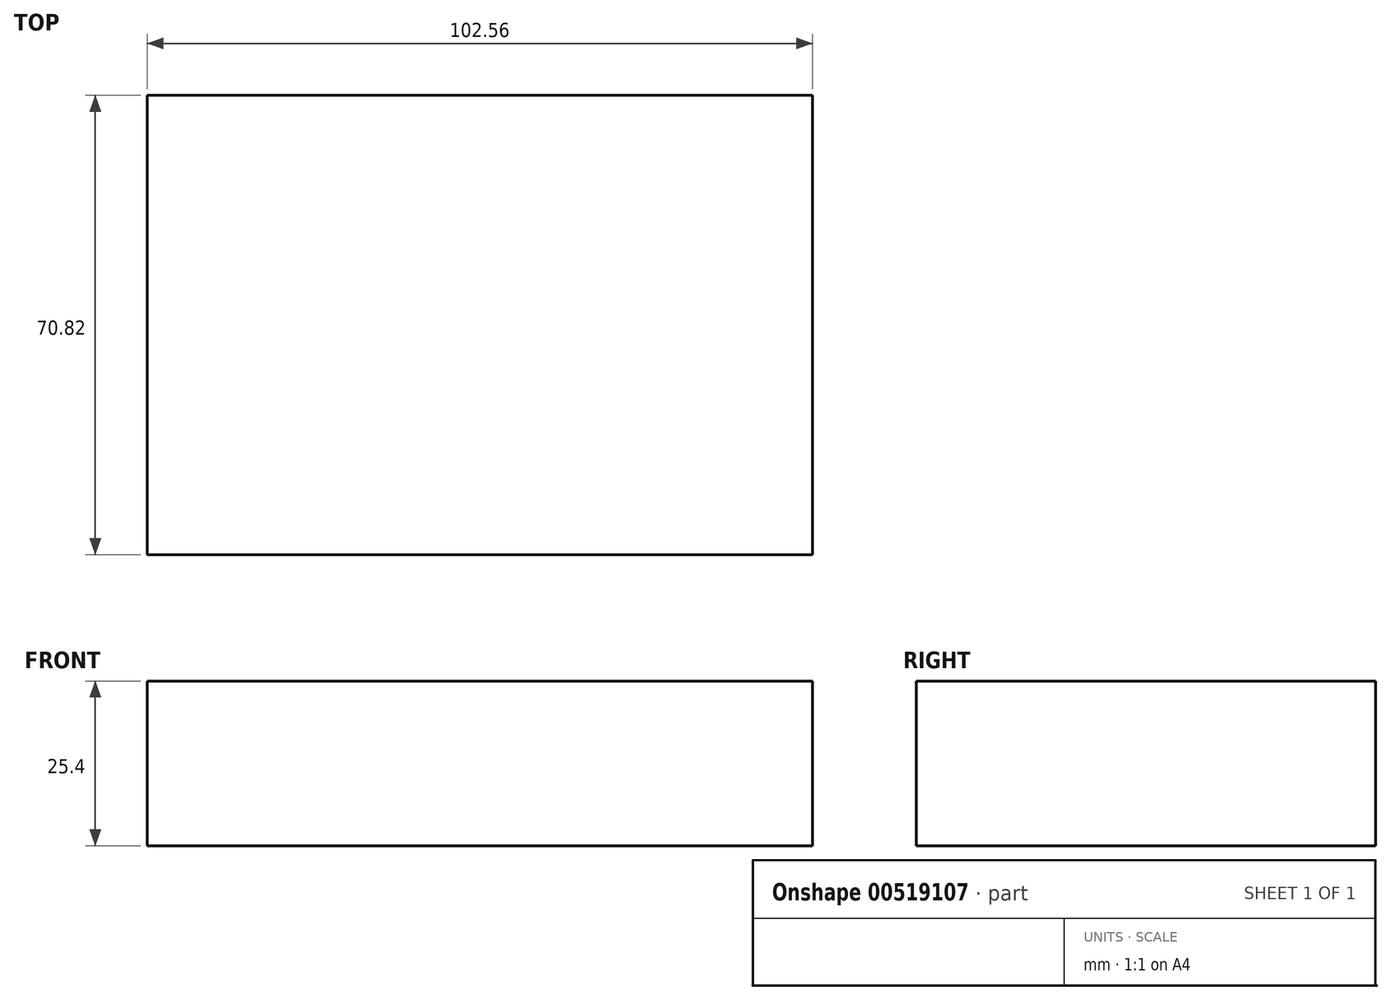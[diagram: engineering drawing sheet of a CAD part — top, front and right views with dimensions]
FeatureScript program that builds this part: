
annotation { "Feature Type Name" : "Feature", "Feature Type Description" : "" }
export const myFeature = defineFeature(function(context is Context, id is Id, definition is map)
    precondition{}
    {
        {
            var Q0;
            Q0=qCreatedBy(makeId("Top.planeOp"),FACE);
            var sketch = newSketch(context, id + "F0", { "sketchPlane" : qUnion([Q0])});
            skLineSegment(sketch, "E0.bottom", {"start": v(51.28, 35.41) * mm, "end": v(-51.28, 35.41) * mm});
            skLineSegment(sketch, "E0.top", {"start": v(51.28, -35.41) * mm, "end": v(-51.28, -35.41) * mm});
            skLineSegment(sketch, "E0.left", {"start": v(51.28, 35.41) * mm, "end": v(51.28, -35.41) * mm});
            skLineSegment(sketch, "E0.right", {"start": v(-51.28, 35.41) * mm, "end": v(-51.28, -35.41) * mm});
            skPoint(sketch, "E0.middle", {"position": v(0, 0) * mm});
            skSolve(sketch);
        }
        {
            var Q0;
            Q0=makeQuery(id+"F0.imprint","IMPRINT",FACE,{"disambiguationData":[TD([[makeQuery(id+"F0.imprint","IMPRINT",EDGE,{"derivedFrom":sQuery(id+"F0.wireOp",EDGE,"E0.bottom")}),1.0]])]});
            extrude(context, id + "F1", {"entities" : qUnion([Q0]), "depth" : 25.4 * mm});
        }
    });
